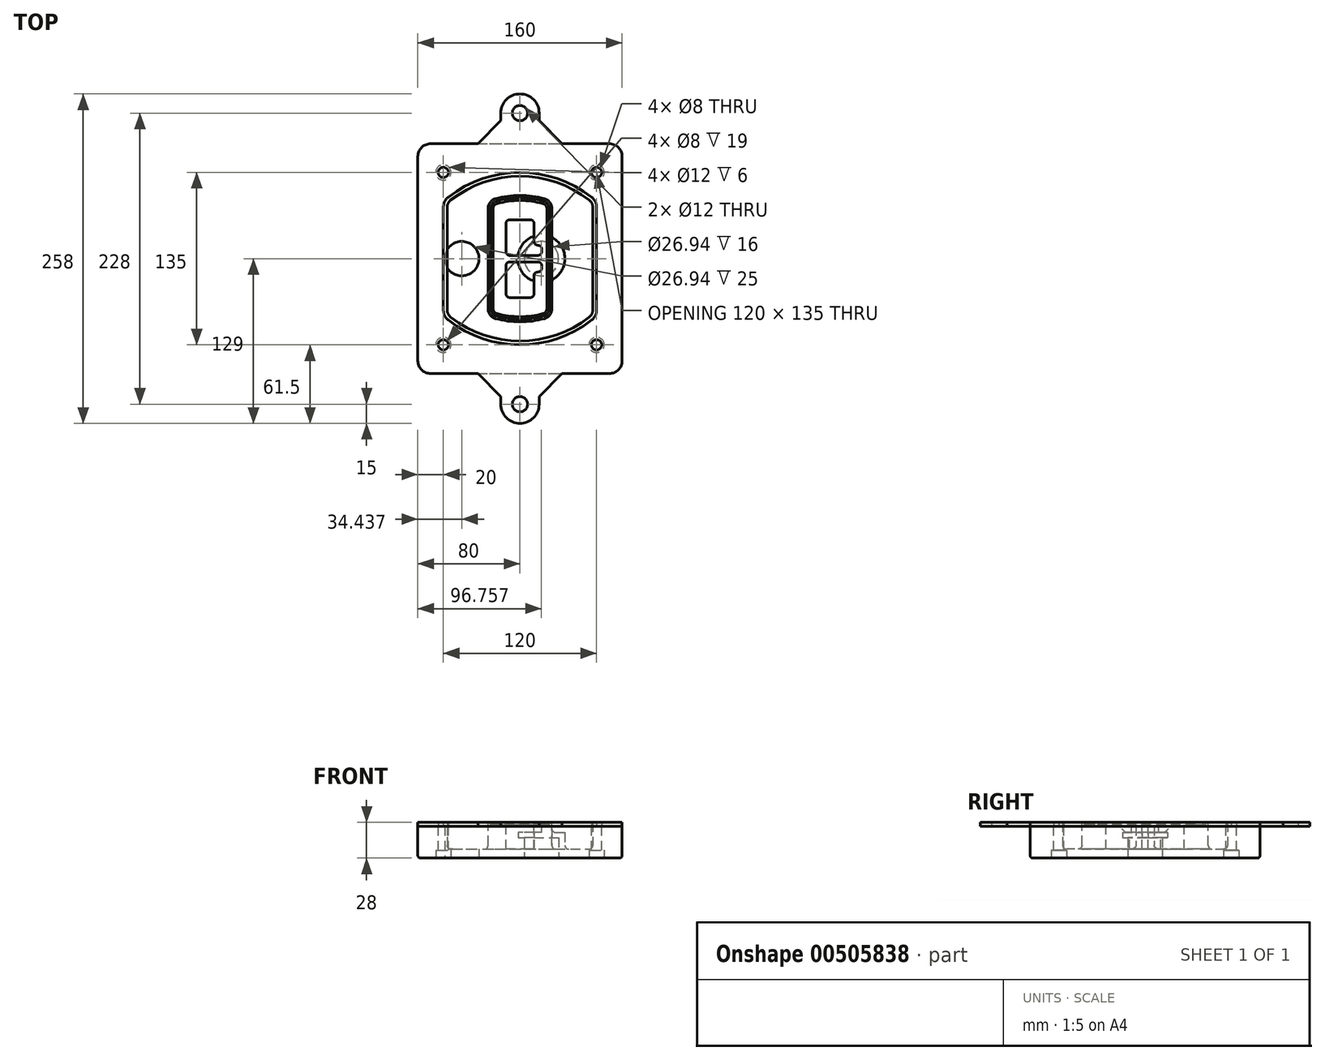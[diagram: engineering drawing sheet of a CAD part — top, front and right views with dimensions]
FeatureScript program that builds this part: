
annotation { "Feature Type Name" : "Feature", "Feature Type Description" : "" }
export const myFeature = defineFeature(function(context is Context, id is Id, definition is map)
    precondition{}
    {
        {
            var Q0;
            Q0=qCreatedBy(makeId("Top.planeOp"),FACE);
            var sketch = newSketch(context, id + "F0", { "sketchPlane" : qUnion([Q0])});
            skPoint(sketch, "E0.rect.middle", {"position": v(0, 0) * mm});
            skLineSegment(sketch, "E1.bottom", {"start": v(-70, -90) * mm, "end": v(70, -90) * mm});
            skLineSegment(sketch, "E1.top", {"start": v(-70, 90) * mm, "end": v(70, 90) * mm});
            skLineSegment(sketch, "E1.left", {"start": v(-80, -80) * mm, "end": v(-80, 80) * mm});
            skLineSegment(sketch, "E1.right", {"start": v(80, -80) * mm, "end": v(80, 80) * mm});
            skLineSegment(sketch, "E2", {"start": v(-80, 90) * mm, "end": v(80, -90) * mm, "construction": true});
            skLineSegment(sketch, "E3", {"start": v(80, 90) * mm, "end": v(-80, -90) * mm, "construction": true});
            skCircle(sketch, "E4", {"center": v(-60, 67.5) * mm, "radius": 4 * mm});
            skCircle(sketch, "E5", {"center": v(60, 67.5) * mm, "radius": 4 * mm});
            skCircle(sketch, "E6", {"center": v(60, -67.5) * mm, "radius": 4 * mm});
            skCircle(sketch, "E7", {"center": v(-60, -67.5) * mm, "radius": 4 * mm});
            skLineSegment(sketch, "E8", {"start": v(-60, 67.5) * mm, "end": v(60, 67.5) * mm, "construction": true});
            skLineSegment(sketch, "E9", {"start": v(60, 67.5) * mm, "end": v(60, -67.5) * mm, "construction": true});
            skLineSegment(sketch, "E10", {"start": v(60, -67.5) * mm, "end": v(-60, -67.5) * mm, "construction": true});
            skLineSegment(sketch, "E11", {"start": v(-60, -67.5) * mm, "end": v(-60, 67.5) * mm, "construction": true});
            skLineSegment(sketch, "E12", {"start": v(-60, 40.3) * mm, "end": v(-60, -40.3) * mm});
            skLineSegment(sketch, "E13", {"start": v(60, 40.3) * mm, "end": v(60, -40.3) * mm});
            skArc(sketch, "E14", {"start": v(56.15, 48.18) * mm, "mid": v(0, 67.5) * mm, "end": v(-56.15, 48.18) * mm});
            skArc(sketch, "E15", {"start": v(-56.15, -48.18) * mm, "mid": v(0, -67.5) * mm, "end": v(56.15, -48.18) * mm});
            skLineSegment(sketch, "E16", {"start": v(-60, 0) * mm, "end": v(60, 0) * mm, "construction": true});
            skPoint(sketch, "E17.visualSharp", {"position": v(-60, -45) * mm});
            skArc(sketch, "E17.filletArc", {"start": v(-60, -40.3) * mm, "mid": v(-58.99, -44.68) * mm, "end": v(-56.15, -48.18) * mm});
            skPoint(sketch, "E18.visualSharp", {"position": v(-60, 45) * mm});
            skArc(sketch, "E18.filletArc", {"start": v(-56.15, 48.18) * mm, "mid": v(-58.99, 44.68) * mm, "end": v(-60, 40.3) * mm});
            skPoint(sketch, "E19.visualSharp", {"position": v(60, 45) * mm});
            skArc(sketch, "E19.filletArc", {"start": v(60, 40.3) * mm, "mid": v(58.99, 44.68) * mm, "end": v(56.15, 48.18) * mm});
            skPoint(sketch, "E20.visualSharp", {"position": v(60, -45) * mm});
            skArc(sketch, "E20.filletArc", {"start": v(56.15, -48.18) * mm, "mid": v(58.99, -44.68) * mm, "end": v(60, -40.3) * mm});
            skPoint(sketch, "E21.visualSharp", {"position": v(-80, 90) * mm});
            skArc(sketch, "E21.filletArc", {"start": v(-70, 90) * mm, "mid": v(-77.07, 87.07) * mm, "end": v(-80, 80) * mm});
            skPoint(sketch, "E22.visualSharp", {"position": v(80, 90) * mm});
            skArc(sketch, "E22.filletArc", {"start": v(80, 80) * mm, "mid": v(77.07, 87.07) * mm, "end": v(70, 90) * mm});
            skPoint(sketch, "E23.visualSharp", {"position": v(80, -90) * mm});
            skArc(sketch, "E23.filletArc", {"start": v(70, -90) * mm, "mid": v(77.07, -87.07) * mm, "end": v(80, -80) * mm});
            skPoint(sketch, "E24.visualSharp", {"position": v(-80, -90) * mm});
            skArc(sketch, "E24.filletArc", {"start": v(-80, -80) * mm, "mid": v(-77.07, -87.07) * mm, "end": v(-70, -90) * mm});
            skArc(sketch, "E25.0", {"start": v(57, 40.3) * mm, "mid": v(56.3, 43.36) * mm, "end": v(54.3, 45.81) * mm});
            skLineSegment(sketch, "E25.1", {"start": v(57, 40.3) * mm, "end": v(57, -40.3) * mm});
            skArc(sketch, "E25.2", {"start": v(54.3, -45.81) * mm, "mid": v(56.3, -43.36) * mm, "end": v(57, -40.3) * mm});
            skArc(sketch, "E25.3", {"start": v(-54.3, -45.81) * mm, "mid": v(0, -64.5) * mm, "end": v(54.3, -45.81) * mm});
            skArc(sketch, "E25.4", {"start": v(-57, -40.3) * mm, "mid": v(-56.3, -43.36) * mm, "end": v(-54.3, -45.81) * mm});
            skArc(sketch, "E25.5", {"start": v(54.3, 45.81) * mm, "mid": v(0, 64.5) * mm, "end": v(-54.3, 45.81) * mm});
            skLineSegment(sketch, "E25.6", {"start": v(-57, 40.3) * mm, "end": v(-57, -40.3) * mm});
            skArc(sketch, "E25.7", {"start": v(-54.3, 45.81) * mm, "mid": v(-56.3, 43.36) * mm, "end": v(-57, 40.3) * mm});
            skArc(sketch, "E26.0", {"start": v(-58.62, 51.33) * mm, "mid": v(-62.58, 46.43) * mm, "end": v(-64, 40.3) * mm});
            skArc(sketch, "E26.1", {"start": v(58.62, 51.33) * mm, "mid": v(0, 71.5) * mm, "end": v(-58.62, 51.33) * mm});
            skArc(sketch, "E26.2", {"start": v(64, 40.3) * mm, "mid": v(62.58, 46.43) * mm, "end": v(58.62, 51.33) * mm});
            skLineSegment(sketch, "E26.3", {"start": v(64, 40.3) * mm, "end": v(64, -40.3) * mm});
            skArc(sketch, "E26.4", {"start": v(58.62, -51.33) * mm, "mid": v(62.58, -46.43) * mm, "end": v(64, -40.3) * mm});
            skLineSegment(sketch, "E26.5", {"start": v(-64, 40.3) * mm, "end": v(-64, -40.3) * mm});
            skArc(sketch, "E26.6", {"start": v(-58.62, -51.33) * mm, "mid": v(0, -71.5) * mm, "end": v(58.62, -51.33) * mm});
            skArc(sketch, "E26.7", {"start": v(-64, -40.3) * mm, "mid": v(-62.58, -46.43) * mm, "end": v(-58.62, -51.33) * mm});
            skSolve(sketch);
        }
        {
            var Q0;
            Q0=makeQuery(id+"F0.imprint","IMPRINT",FACE,{"disambiguationData":[TD([[makeQuery(id+"F0.imprint","IMPRINT",EDGE,{"derivedFrom":sQuery(id+"F0.wireOp",EDGE,"E1.bottom")}),1.0]])]});
            var Q1;
            Q1=makeQuery(id+"F0.imprint","IMPRINT",FACE,{"disambiguationData":[TD([[makeQuery(id+"F0.imprint","IMPRINT",EDGE,{"derivedFrom":sQuery(id+"F0.wireOp",EDGE,"E12")}),1.0]])]});
            var Q2;
            Q2=makeQuery(id+"F0.imprint","IMPRINT",FACE,{"disambiguationData":[TD([[makeQuery(id+"F0.imprint","IMPRINT",EDGE,{"derivedFrom":sQuery(id+"F0.wireOp",EDGE,"E25.0")}),1.0]])]});
            var Q3;
            Q3=makeQuery(id+"F0.imprint","IMPRINT",FACE,{"disambiguationData":[TD([[makeQuery(id+"F0.imprint","IMPRINT",EDGE,{"derivedFrom":sQuery(id+"F0.wireOp",EDGE,"E12")}),-1.0]])]});
            extrude(context, id + "F1", {"entities" : qUnion([Q0, Q1, Q2, Q3]), "oppositeDirection" : true, "depth" : 25 * mm});
        }
        {
            var Q0;
            Q0=makeQuery(id+"F0.imprint","IMPRINT",FACE,{"disambiguationData":[TD([[makeQuery(id+"F0.imprint","IMPRINT",EDGE,{"derivedFrom":sQuery(id+"F0.wireOp",EDGE,"E12")}),1.0]])]});
            extrude(context, id + "F2", {"entities" : qUnion([Q0]), "operationType" : NewBodyOperationType.ADD, "depth" : 3 * mm});
        }
        {
            var Q0;
            Q0=makeQuery(id+"F0.imprint","IMPRINT",FACE,{"disambiguationData":[TD([[makeQuery(id+"F0.imprint","IMPRINT",EDGE,{"derivedFrom":sQuery(id+"F0.wireOp",EDGE,"E25.0")}),1.0]])]});
            extrude(context, id + "F3", {"entities" : qUnion([Q0]), "operationType" : NewBodyOperationType.REMOVE, "oppositeDirection" : true, "depth" : 18 * mm});
        }
        {
            var Q0;
            Q0=makeQuery(id+"F2.opExtrude","CAP_FACE",FACE,{"disambiguationData":[OSD([sQuery(id+"F0.wireOp",EDGE,"E12"),sQuery(id+"F0.wireOp",EDGE,"E13"),sQuery(id+"F0.wireOp",EDGE,"E14"),sQuery(id+"F0.wireOp",EDGE,"E15"),sQuery(id+"F0.wireOp",EDGE,"E17.filletArc"),sQuery(id+"F0.wireOp",EDGE,"E18.filletArc"),sQuery(id+"F0.wireOp",EDGE,"E19.filletArc"),sQuery(id+"F0.wireOp",EDGE,"E20.filletArc"),sQuery(id+"F0.wireOp",EDGE,"E25.0"),sQuery(id+"F0.wireOp",EDGE,"E25.1"),sQuery(id+"F0.wireOp",EDGE,"E25.2"),sQuery(id+"F0.wireOp",EDGE,"E25.3"),sQuery(id+"F0.wireOp",EDGE,"E25.4"),sQuery(id+"F0.wireOp",EDGE,"E25.5"),sQuery(id+"F0.wireOp",EDGE,"E25.6"),sQuery(id+"F0.wireOp",EDGE,"E25.7")])],"isStart":false});
            var sketch = newSketch(context, id + "F4", { "sketchPlane" : qUnion([Q0])});
            skArc(sketch, "E27.0", {"start": v(-19.08, -46.97) * mm, "mid": v(0, -49.5) * mm, "end": v(19.08, -46.97) * mm});
            skArc(sketch, "E28.0", {"start": v(19.08, 46.97) * mm, "mid": v(0, 49.5) * mm, "end": v(-19.08, 46.97) * mm});
            skLineSegment(sketch, "E29", {"start": v(-25, 39.25) * mm, "end": v(-25, -39.25) * mm});
            skLineSegment(sketch, "E30", {"start": v(25, 39.25) * mm, "end": v(25, -39.25) * mm});
            skLineSegment(sketch, "E31", {"start": v(-25, 45.1) * mm, "end": v(25, 45.1) * mm, "construction": true});
            skLineSegment(sketch, "E32", {"start": v(-25, -45.1) * mm, "end": v(25, -45.1) * mm, "construction": true});
            skPoint(sketch, "E33.visualSharp", {"position": v(-25, 45.1) * mm});
            skArc(sketch, "E33.filletArc", {"start": v(-19.08, 46.97) * mm, "mid": v(-23.35, 44.11) * mm, "end": v(-25, 39.25) * mm});
            skPoint(sketch, "E34.visualSharp", {"position": v(25, 45.1) * mm});
            skArc(sketch, "E34.filletArc", {"start": v(25, 39.25) * mm, "mid": v(23.35, 44.11) * mm, "end": v(19.08, 46.97) * mm});
            skPoint(sketch, "E35.visualSharp", {"position": v(25, -45.1) * mm});
            skArc(sketch, "E35.filletArc", {"start": v(19.08, -46.97) * mm, "mid": v(23.35, -44.11) * mm, "end": v(25, -39.25) * mm});
            skPoint(sketch, "E36.visualSharp", {"position": v(-25, -45.1) * mm});
            skArc(sketch, "E36.filletArc", {"start": v(-25, -39.25) * mm, "mid": v(-23.35, -44.11) * mm, "end": v(-19.08, -46.97) * mm});
            skArc(sketch, "E37.0", {"start": v(54.3, 45.81) * mm, "mid": v(0, 64.5) * mm, "end": v(-54.3, 45.81) * mm});
            skArc(sketch, "E37.1", {"start": v(-54.3, 45.81) * mm, "mid": v(-56.3, 43.36) * mm, "end": v(-57, 40.3) * mm});
            skLineSegment(sketch, "E37.2", {"start": v(-57, 40.3) * mm, "end": v(-57, -40.3) * mm});
            skArc(sketch, "E37.3", {"start": v(-57, -40.3) * mm, "mid": v(-56.3, -43.36) * mm, "end": v(-54.3, -45.81) * mm});
            skArc(sketch, "E37.4", {"start": v(-54.3, -45.81) * mm, "mid": v(0, -64.5) * mm, "end": v(54.3, -45.81) * mm});
            skArc(sketch, "E37.5", {"start": v(54.3, -45.81) * mm, "mid": v(56.3, -43.36) * mm, "end": v(57, -40.3) * mm});
            skLineSegment(sketch, "E37.6", {"start": v(57, 40.3) * mm, "end": v(57, -40.3) * mm});
            skArc(sketch, "E37.7", {"start": v(57, 40.3) * mm, "mid": v(56.3, 43.36) * mm, "end": v(54.3, 45.81) * mm});
            skLineSegment(sketch, "E38.0", {"start": v(23, 39.25) * mm, "end": v(23, -39.25) * mm});
            skArc(sketch, "E38.1", {"start": v(18.56, -45.04) * mm, "mid": v(21.76, -42.9) * mm, "end": v(23, -39.25) * mm});
            skArc(sketch, "E38.2", {"start": v(-18.56, -45.04) * mm, "mid": v(0, -47.5) * mm, "end": v(18.56, -45.04) * mm});
            skArc(sketch, "E38.3", {"start": v(-23, -39.25) * mm, "mid": v(-21.76, -42.9) * mm, "end": v(-18.56, -45.04) * mm});
            skLineSegment(sketch, "E38.4", {"start": v(-23, 39.25) * mm, "end": v(-23, -39.25) * mm});
            skArc(sketch, "E38.5", {"start": v(23, 39.25) * mm, "mid": v(21.76, 42.9) * mm, "end": v(18.56, 45.04) * mm});
            skArc(sketch, "E38.6", {"start": v(-18.56, 45.04) * mm, "mid": v(-21.76, 42.9) * mm, "end": v(-23, 39.25) * mm});
            skArc(sketch, "E38.7", {"start": v(18.56, 45.04) * mm, "mid": v(0, 47.5) * mm, "end": v(-18.56, 45.04) * mm});
            skArc(sketch, "E39.0", {"start": v(21, 39.25) * mm, "mid": v(20.18, 41.68) * mm, "end": v(18.04, 43.1) * mm});
            skLineSegment(sketch, "E39.1", {"start": v(21, 39.25) * mm, "end": v(21, -39.25) * mm});
            skArc(sketch, "E39.2", {"start": v(18.04, -43.1) * mm, "mid": v(20.18, -41.68) * mm, "end": v(21, -39.25) * mm});
            skArc(sketch, "E39.3", {"start": v(-18.04, -43.1) * mm, "mid": v(0, -45.5) * mm, "end": v(18.04, -43.1) * mm});
            skArc(sketch, "E39.4", {"start": v(-21, -39.25) * mm, "mid": v(-20.18, -41.68) * mm, "end": v(-18.04, -43.1) * mm});
            skArc(sketch, "E39.5", {"start": v(18.04, 43.1) * mm, "mid": v(0, 45.5) * mm, "end": v(-18.04, 43.1) * mm});
            skLineSegment(sketch, "E39.6", {"start": v(-21, 39.25) * mm, "end": v(-21, -39.25) * mm});
            skArc(sketch, "E39.7", {"start": v(-18.04, 43.1) * mm, "mid": v(-20.18, 41.68) * mm, "end": v(-21, 39.25) * mm});
            skLineSegment(sketch, "E40", {"start": v(-25, 0) * mm, "end": v(25, 0) * mm, "construction": true});
            skLineSegment(sketch, "E41", {"start": v(-11, 5.5) * mm, "end": v(-11, 27.5) * mm});
            skLineSegment(sketch, "E42", {"start": v(-8, 30.5) * mm, "end": v(8, 30.5) * mm});
            skLineSegment(sketch, "E43", {"start": v(11, 27.5) * mm, "end": v(11, 13.5) * mm});
            skLineSegment(sketch, "E44", {"start": v(14, 10.5) * mm, "end": v(14, 10.5) * mm});
            skLineSegment(sketch, "E45", {"start": v(17, 7.5) * mm, "end": v(17, 5.5) * mm});
            skLineSegment(sketch, "E46", {"start": v(14, 2.5) * mm, "end": v(-8, 2.5) * mm});
            skPoint(sketch, "E47.visualSharp", {"position": v(-11, 30.5) * mm});
            skArc(sketch, "E47.filletArc", {"start": v(-8, 30.5) * mm, "mid": v(-10.12, 29.62) * mm, "end": v(-11, 27.5) * mm});
            skPoint(sketch, "E48.visualSharp", {"position": v(11, 30.5) * mm});
            skArc(sketch, "E48.filletArc", {"start": v(11, 27.5) * mm, "mid": v(10.12, 29.62) * mm, "end": v(8, 30.5) * mm});
            skPoint(sketch, "E49.visualSharp", {"position": v(11, 10.5) * mm});
            skArc(sketch, "E49.filletArc", {"start": v(11, 13.5) * mm, "mid": v(11.88, 11.38) * mm, "end": v(14, 10.5) * mm});
            skPoint(sketch, "E50.visualSharp", {"position": v(17, 10.5) * mm});
            skArc(sketch, "E50.filletArc", {"start": v(17, 7.5) * mm, "mid": v(16.12, 9.62) * mm, "end": v(14, 10.5) * mm});
            skPoint(sketch, "E51.visualSharp", {"position": v(17, 2.5) * mm});
            skArc(sketch, "E51.filletArc", {"start": v(14, 2.5) * mm, "mid": v(16.12, 3.38) * mm, "end": v(17, 5.5) * mm});
            skPoint(sketch, "E52.visualSharp", {"position": v(-11, 2.5) * mm});
            skArc(sketch, "E52.filletArc", {"start": v(-11, 5.5) * mm, "mid": v(-10.12, 3.38) * mm, "end": v(-8, 2.5) * mm});
            skLineSegment(sketch, "E53.0.MirrorCS", {"start": v(14, -2.5) * mm, "end": v(-8, -2.5) * mm});
            skArc(sketch, "E54.0.MirrorCS", {"start": v(-11, -5.5) * mm, "mid": v(-10.12, -3.38) * mm, "end": v(-8, -2.5) * mm});
            skLineSegment(sketch, "E55.0.MirrorCS", {"start": v(-11, -5.5) * mm, "end": v(-11, -27.5) * mm});
            skArc(sketch, "E56.0.MirrorCS", {"start": v(-8, -30.5) * mm, "mid": v(-10.12, -29.62) * mm, "end": v(-11, -27.5) * mm});
            skLineSegment(sketch, "E57.0.MirrorCS", {"start": v(-8, -30.5) * mm, "end": v(8, -30.5) * mm});
            skArc(sketch, "E58.0.MirrorCS", {"start": v(11, -27.5) * mm, "mid": v(10.12, -29.62) * mm, "end": v(8, -30.5) * mm});
            skLineSegment(sketch, "E59.0.MirrorCS", {"start": v(11, -27.5) * mm, "end": v(11, -13.5) * mm});
            skArc(sketch, "E60.0.MirrorCS", {"start": v(11, -13.5) * mm, "mid": v(11.88, -11.38) * mm, "end": v(14, -10.5) * mm});
            skArc(sketch, "E61.0.MirrorCS", {"start": v(17, -7.5) * mm, "mid": v(16.12, -9.62) * mm, "end": v(14, -10.5) * mm});
            skLineSegment(sketch, "E62.0.MirrorCS", {"start": v(17, -7.5) * mm, "end": v(17, -5.5) * mm});
            skArc(sketch, "E63.0.MirrorCS", {"start": v(14, -2.5) * mm, "mid": v(16.12, -3.38) * mm, "end": v(17, -5.5) * mm});
            skSolve(sketch);
        }
        {
            var Q0;
            Q0=makeQuery(id+"F4.imprint","IMPRINT",FACE,{"disambiguationData":[TD([[makeQuery(id+"F4.imprint","IMPRINT",EDGE,{"derivedFrom":sQuery(id+"F4.wireOp",EDGE,"E27.0")}),1.0]])]});
            var Q1;
            Q1=makeQuery(id+"F4.imprint","IMPRINT",FACE,{"disambiguationData":[TD([[makeQuery(id+"F4.imprint","IMPRINT",EDGE,{"derivedFrom":sQuery(id+"F4.wireOp",EDGE,"E38.0")}),-1.0]])]});
            var Q2;
            Q2=makeQuery(id+"F4.imprint","IMPRINT",FACE,{"disambiguationData":[TD([[makeQuery(id+"F4.imprint","IMPRINT",EDGE,{"derivedFrom":sQuery(id+"F4.wireOp",EDGE,"E39.0")}),1.0]])]});
            extrude(context, id + "F5", {"entities" : qUnion([Q0, Q1, Q2]), "operationType" : NewBodyOperationType.ADD, "endBound" : BoundingType.UP_TO_NEXT, "oppositeDirection" : true, "depth" : 25 * mm});
        }
        {
            var Q0;
            Q0=makeQuery(id+"F4.imprint","IMPRINT",FACE,{"disambiguationData":[TD([[makeQuery(id+"F4.imprint","IMPRINT",EDGE,{"derivedFrom":sQuery(id+"F4.wireOp",EDGE,"E38.0")}),-1.0]])]});
            extrude(context, id + "F6", {"entities" : qUnion([Q0]), "operationType" : NewBodyOperationType.REMOVE, "oppositeDirection" : true, "depth" : 2 * mm});
        }
        {
            var Q0;
            Q0=makeQuery(id+"F1.opExtrude","CAP_FACE",FACE,{"disambiguationData":[OSD([sQuery(id+"F0.wireOp",EDGE,"E1.bottom"),sQuery(id+"F0.wireOp",EDGE,"E1.top"),sQuery(id+"F0.wireOp",EDGE,"E1.left"),sQuery(id+"F0.wireOp",EDGE,"E1.right"),sQuery(id+"F0.wireOp",EDGE,"E4"),sQuery(id+"F0.wireOp",EDGE,"E5"),sQuery(id+"F0.wireOp",EDGE,"E6"),sQuery(id+"F0.wireOp",EDGE,"E7"),sQuery(id+"F0.wireOp",EDGE,"E21.filletArc"),sQuery(id+"F0.wireOp",EDGE,"E22.filletArc"),sQuery(id+"F0.wireOp",EDGE,"E23.filletArc"),sQuery(id+"F0.wireOp",EDGE,"E24.filletArc")])],"isStart":false});
            var sketch = newSketch(context, id + "F7", { "sketchPlane" : qUnion([Q0])});
            skCircle(sketch, "E64", {"center": v(16.76, 0) * mm, "radius": 13.47 * mm});
            skCircle(sketch, "E65", {"center": v(-45.56, 0) * mm, "radius": 13.47 * mm});
            skLineSegment(sketch, "E66", {"start": v(80, 0) * mm, "end": v(-80, 0) * mm});
            skCircle(sketch, "E67", {"center": v(16.76, 0) * mm, "radius": 18.47 * mm});
            skCircle(sketch, "E68", {"center": v(60, -67.5) * mm, "radius": 6 * mm});
            skCircle(sketch, "E69", {"center": v(-60, -67.5) * mm, "radius": 6 * mm});
            skCircle(sketch, "E70", {"center": v(-60, 67.5) * mm, "radius": 6 * mm});
            skCircle(sketch, "E71", {"center": v(60, 67.5) * mm, "radius": 6 * mm});
            skSolve(sketch);
        }
        {
            var Q0;
            {var subQ1=sQuery(id+"F7.wireOp",EDGE,"E66");var subQ4=sQuery(id+"F7.wireOp",EDGE,"E64");var subQ6=makeQuery(id+"F7.imprint","INTERSECT",VERTEX,{"disambiguationData":[OD(0.0)],"derivedFrom":[subQ4,subQ1]});Q0=makeQuery(id+"F7.imprint","IMPRINT",FACE,{"disambiguationData":[TD([[makeQuery(id+"F7.imprint","IMPRINT",EDGE,{"disambiguationData":[TD([[subQ6,-1.0]])],"derivedFrom":subQ4}),-1.0]])]});}
            var Q1;
            {var subQ0=sQuery(id+"F7.wireOp",EDGE,"E66");var subQ1=sQuery(id+"F7.wireOp",EDGE,"E64");var subQ3=makeQuery(id+"F7.imprint","INTERSECT",VERTEX,{"disambiguationData":[OD(0.0)],"derivedFrom":[subQ1,subQ0]});Q1=makeQuery(id+"F7.imprint","IMPRINT",FACE,{"disambiguationData":[TD([[makeQuery(id+"F7.imprint","IMPRINT",EDGE,{"disambiguationData":[TD([[subQ3,-1.0]])],"derivedFrom":subQ1}),1.0]])]});}
            var Q2;
            {var subQ0=sQuery(id+"F7.wireOp",EDGE,"E66");var subQ1=sQuery(id+"F7.wireOp",EDGE,"E64");var subQ3=makeQuery(id+"F7.imprint","INTERSECT",VERTEX,{"disambiguationData":[OD(0.0)],"derivedFrom":[subQ1,subQ0]});Q2=makeQuery(id+"F7.imprint","IMPRINT",FACE,{"disambiguationData":[TD([[makeQuery(id+"F7.imprint","IMPRINT",EDGE,{"disambiguationData":[TD([[subQ3,1.0]])],"derivedFrom":subQ1}),1.0]])]});}
            var Q3;
            {var subQ1=sQuery(id+"F7.wireOp",EDGE,"E66");var subQ4=sQuery(id+"F7.wireOp",EDGE,"E64");var subQ6=makeQuery(id+"F7.imprint","INTERSECT",VERTEX,{"disambiguationData":[OD(0.0)],"derivedFrom":[subQ4,subQ1]});Q3=makeQuery(id+"F7.imprint","IMPRINT",FACE,{"disambiguationData":[TD([[makeQuery(id+"F7.imprint","IMPRINT",EDGE,{"disambiguationData":[TD([[subQ6,1.0]])],"derivedFrom":subQ4}),-1.0]])]});}
            extrude(context, id + "F8", {"entities" : qUnion([Q0, Q1, Q2, Q3]), "operationType" : NewBodyOperationType.ADD, "oppositeDirection" : true, "depth" : 20 * mm});
        }
        {
            var Q0;
            {var subQ0=sQuery(id+"F7.wireOp",EDGE,"E66");var subQ1=sQuery(id+"F7.wireOp",EDGE,"E64");var subQ3=makeQuery(id+"F7.imprint","INTERSECT",VERTEX,{"disambiguationData":[OD(0.0)],"derivedFrom":[subQ1,subQ0]});Q0=makeQuery(id+"F7.imprint","IMPRINT",FACE,{"disambiguationData":[TD([[makeQuery(id+"F7.imprint","IMPRINT",EDGE,{"disambiguationData":[TD([[subQ3,-1.0]])],"derivedFrom":subQ1}),1.0]])]});}
            var Q1;
            {var subQ0=sQuery(id+"F7.wireOp",EDGE,"E66");var subQ1=sQuery(id+"F7.wireOp",EDGE,"E64");var subQ3=makeQuery(id+"F7.imprint","INTERSECT",VERTEX,{"disambiguationData":[OD(0.0)],"derivedFrom":[subQ1,subQ0]});Q1=makeQuery(id+"F7.imprint","IMPRINT",FACE,{"disambiguationData":[TD([[makeQuery(id+"F7.imprint","IMPRINT",EDGE,{"disambiguationData":[TD([[subQ3,1.0]])],"derivedFrom":subQ1}),1.0]])]});}
            extrude(context, id + "F9", {"entities" : qUnion([Q0, Q1]), "operationType" : NewBodyOperationType.REMOVE, "oppositeDirection" : true, "depth" : 16 * mm});
        }
        {
            var Q0;
            {var subQ0=sQuery(id+"F7.wireOp",EDGE,"E66");var subQ1=sQuery(id+"F7.wireOp",EDGE,"E65");var subQ3=makeQuery(id+"F7.imprint","INTERSECT",VERTEX,{"disambiguationData":[OD(0.0)],"derivedFrom":[subQ1,subQ0]});Q0=makeQuery(id+"F7.imprint","IMPRINT",FACE,{"disambiguationData":[TD([[makeQuery(id+"F7.imprint","IMPRINT",EDGE,{"disambiguationData":[TD([[subQ3,-1.0]])],"derivedFrom":subQ1}),1.0]])]});}
            var Q1;
            {var subQ0=sQuery(id+"F7.wireOp",EDGE,"E66");var subQ1=sQuery(id+"F7.wireOp",EDGE,"E65");var subQ3=makeQuery(id+"F7.imprint","INTERSECT",VERTEX,{"disambiguationData":[OD(0.0)],"derivedFrom":[subQ1,subQ0]});Q1=makeQuery(id+"F7.imprint","IMPRINT",FACE,{"disambiguationData":[TD([[makeQuery(id+"F7.imprint","IMPRINT",EDGE,{"disambiguationData":[TD([[subQ3,1.0]])],"derivedFrom":subQ1}),1.0]])]});}
            extrude(context, id + "F10", {"entities" : qUnion([Q0, Q1]), "operationType" : NewBodyOperationType.REMOVE, "oppositeDirection" : true, "depth" : 25 * mm});
        }
        {
            var Q0;
            Q0=makeQuery(id+"F7.imprint","IMPRINT",FACE,{"disambiguationData":[TD([[makeQuery(id+"F7.imprint","IMPRINT",EDGE,{"derivedFrom":sQuery(id+"F7.wireOp",EDGE,"E68")}),1.0]])]});
            var Q1;
            Q1=makeQuery(id+"F7.imprint","IMPRINT",FACE,{"disambiguationData":[TD([[makeQuery(id+"F7.imprint","IMPRINT",EDGE,{"derivedFrom":makeQuery(id+"F1.opExtrude","CAP_EDGE",EDGE,{"disambiguationData":[OSD([sQuery(id+"F0.wireOp",EDGE,"E5")])],"isStart":false})}),-1.0]])]});
            var Q2;
            Q2=makeQuery(id+"F7.imprint","IMPRINT",FACE,{"disambiguationData":[TD([[makeQuery(id+"F7.imprint","IMPRINT",EDGE,{"derivedFrom":sQuery(id+"F7.wireOp",EDGE,"E69")}),1.0]])]});
            var Q3;
            Q3=makeQuery(id+"F7.imprint","IMPRINT",FACE,{"disambiguationData":[TD([[makeQuery(id+"F7.imprint","IMPRINT",EDGE,{"derivedFrom":makeQuery(id+"F1.opExtrude","CAP_EDGE",EDGE,{"disambiguationData":[OSD([sQuery(id+"F0.wireOp",EDGE,"E4")])],"isStart":false})}),-1.0]])]});
            var Q4;
            Q4=makeQuery(id+"F7.imprint","IMPRINT",FACE,{"disambiguationData":[TD([[makeQuery(id+"F7.imprint","IMPRINT",EDGE,{"derivedFrom":sQuery(id+"F7.wireOp",EDGE,"E70")}),1.0]])]});
            var Q5;
            Q5=makeQuery(id+"F7.imprint","IMPRINT",FACE,{"disambiguationData":[TD([[makeQuery(id+"F7.imprint","IMPRINT",EDGE,{"derivedFrom":makeQuery(id+"F1.opExtrude","CAP_EDGE",EDGE,{"disambiguationData":[OSD([sQuery(id+"F0.wireOp",EDGE,"E7")])],"isStart":false})}),-1.0]])]});
            var Q6;
            Q6=makeQuery(id+"F7.imprint","IMPRINT",FACE,{"disambiguationData":[TD([[makeQuery(id+"F7.imprint","IMPRINT",EDGE,{"derivedFrom":sQuery(id+"F7.wireOp",EDGE,"E71")}),1.0]])]});
            var Q7;
            Q7=makeQuery(id+"F7.imprint","IMPRINT",FACE,{"disambiguationData":[TD([[makeQuery(id+"F7.imprint","IMPRINT",EDGE,{"derivedFrom":makeQuery(id+"F1.opExtrude","CAP_EDGE",EDGE,{"disambiguationData":[OSD([sQuery(id+"F0.wireOp",EDGE,"E6")])],"isStart":false})}),-1.0]])]});
            extrude(context, id + "F11", {"entities" : qUnion([Q0, Q1, Q2, Q3, Q4, Q5, Q6, Q7]), "operationType" : NewBodyOperationType.REMOVE, "oppositeDirection" : true, "depth" : 6 * mm});
        }
        {
            var Q0;
            Q0=makeQuery(id+"F9.boolean.opBoolean","COPY",FACE,{"derivedFrom":makeQuery(id+"F9.opExtrude","CAP_FACE",FACE,{"disambiguationData":[OSD([sQuery(id+"F7.wireOp",EDGE,"E64")])],"isStart":false})});
            var sketch = newSketch(context, id + "F12", { "sketchPlane" : qUnion([Q0])});
            skArc(sketch, "E72.0", {"start": v(11, 17.55) * mm, "mid": v(2.57, 11.82) * mm, "end": v(-1.54, 2.5) * mm});
            skArc(sketch, "E72.1", {"start": v(-1.54, -2.5) * mm, "mid": v(2.57, -11.82) * mm, "end": v(11, -17.55) * mm});
            skLineSegment(sketch, "E73", {"start": v(-1.54, -2.5) * mm, "end": v(14, -2.5) * mm});
            skLineSegment(sketch, "E74.0", {"start": v(14, 2.5) * mm, "end": v(-1.54, 2.5) * mm});
            skArc(sketch, "E74.1", {"start": v(14, 2.5) * mm, "mid": v(16.12, 3.38) * mm, "end": v(17, 5.5) * mm});
            skLineSegment(sketch, "E74.2", {"start": v(17, 7.5) * mm, "end": v(17, 5.5) * mm});
            skArc(sketch, "E74.3", {"start": v(17, 7.5) * mm, "mid": v(16.12, 9.62) * mm, "end": v(14, 10.5) * mm});
            skArc(sketch, "E74.4", {"start": v(11, 13.5) * mm, "mid": v(11.88, 11.38) * mm, "end": v(14, 10.5) * mm});
            skLineSegment(sketch, "E74.5", {"start": v(11, 17.55) * mm, "end": v(11, 13.5) * mm});
            skLineSegment(sketch, "E74.7", {"start": v(14, -2.5) * mm, "end": v(-1.54, -2.5) * mm});
            skArc(sketch, "E74.8", {"start": v(14, -2.5) * mm, "mid": v(16.12, -3.38) * mm, "end": v(17, -5.5) * mm});
            skLineSegment(sketch, "E74.9", {"start": v(17, -7.5) * mm, "end": v(17, -5.5) * mm});
            skArc(sketch, "E74.10", {"start": v(17, -7.5) * mm, "mid": v(16.12, -9.62) * mm, "end": v(14, -10.5) * mm});
            skArc(sketch, "E74.11", {"start": v(11, -13.5) * mm, "mid": v(11.88, -11.38) * mm, "end": v(14, -10.5) * mm});
            skLineSegment(sketch, "E74.12", {"start": v(11, -17.55) * mm, "end": v(11, -13.5) * mm});
            skPoint(sketch, "E75.orphan", {"position": v(11, -27.5) * mm});
            skPoint(sketch, "E76.orphan", {"position": v(-8, -2.5) * mm});
            skPoint(sketch, "E77.orphan", {"position": v(-8, 2.5) * mm});
            skPoint(sketch, "E78.orphan", {"position": v(11, 27.5) * mm});
            skSolve(sketch);
        }
        {
            var Q0;
            {var subQ7=sQuery(id+"F12.wireOp",EDGE,"E72.0");var subQ14=sQuery(id+"F12.wireOp",EDGE,"E72.1");var subQ16=sQuery(id+"F12.wireOp",EDGE,"E74.1");var subQ18=sQuery(id+"F12.wireOp",EDGE,"E74.8");Q0=qUnion([makeQuery(id+"F12.imprint","IMPRINT",FACE,{"disambiguationData":[TD([[makeQuery(id+"F12.imprint","IMPRINT",EDGE,{"derivedFrom":subQ7}),1.0]])]}),makeQuery(id+"F12.imprint","IMPRINT",FACE,{"disambiguationData":[TD([[makeQuery(id+"F12.imprint","IMPRINT",EDGE,{"derivedFrom":subQ14}),1.0]])]}),makeQuery(id+"F12.imprint","IMPRINT",FACE,{"disambiguationData":[TD([[makeQuery(id+"F12.imprint","IMPRINT",EDGE,{"derivedFrom":subQ16}),1.0]])]}),makeQuery(id+"F12.imprint","IMPRINT",FACE,{"disambiguationData":[TD([[makeQuery(id+"F12.imprint","IMPRINT",EDGE,{"derivedFrom":subQ18}),-1.0]])]})]);}
            var Q1;
            Q1=makeQuery(id+"F5.boolean.opBoolean","SPLIT",FACE,{"disambiguationData":[TD([makeQuery(id+"F5.opExtrude","SWEPT_FACE",FACE,{"disambiguationData":[OSD([sQuery(id+"F4.wireOp",EDGE,"E41")])]})])],"derivedFrom":makeQuery(id+"F3.boolean.opBoolean","COPY",FACE,{"derivedFrom":makeQuery(id+"F3.opExtrude","CAP_FACE",FACE,{"disambiguationData":[OSD([sQuery(id+"F0.wireOp",EDGE,"E25.0"),sQuery(id+"F0.wireOp",EDGE,"E25.1"),sQuery(id+"F0.wireOp",EDGE,"E25.2"),sQuery(id+"F0.wireOp",EDGE,"E25.3"),sQuery(id+"F0.wireOp",EDGE,"E25.4"),sQuery(id+"F0.wireOp",EDGE,"E25.5"),sQuery(id+"F0.wireOp",EDGE,"E25.6"),sQuery(id+"F0.wireOp",EDGE,"E25.7")])],"isStart":false})})});
            extrude(context, id + "F13", {"entities" : qUnion([Q0]), "operationType" : NewBodyOperationType.REMOVE, "endBound" : BoundingType.UP_TO_SURFACE, "endBoundEntityFace" : qUnion([Q1]), "depth" : 25 * mm});
        }
        {
            var Q0;
            Q0=makeQuery(id+"F3.boolean.opBoolean","COPY",EDGE,{"derivedFrom":makeQuery(id+"F3.opExtrude","CAP_EDGE",EDGE,{"disambiguationData":[OSD([sQuery(id+"F0.wireOp",EDGE,"E25.6")])],"isStart":false})});
            var Q1;
            Q1=makeQuery(id+"F8.boolean.opBoolean","INTERSECT",EDGE,{"derivedFrom":[makeQuery(id+"F5.opExtrude","SWEPT_FACE",FACE,{"disambiguationData":[OSD([sQuery(id+"F4.wireOp",EDGE,"E30")])]}),makeQuery(id+"F8.opExtrude","CAP_FACE",FACE,{"disambiguationData":[OSD([sQuery(id+"F7.wireOp",EDGE,"E67")])],"isStart":false})]});
            var Q2;
            Q2=makeQuery(id+"F8.boolean.opBoolean","INTERSECT",EDGE,{"disambiguationData":[OD(1.0)],"derivedFrom":[makeQuery(id+"F5.opExtrude","SWEPT_FACE",FACE,{"disambiguationData":[OSD([sQuery(id+"F4.wireOp",EDGE,"E30")])]}),makeQuery(id+"F8.opExtrude","SWEPT_FACE",FACE,{"disambiguationData":[OSD([sQuery(id+"F7.wireOp",EDGE,"E67")])]})]});
            var Q3;
            {var subQ0=sQuery(id+"F4.wireOp",EDGE,"E30");Q3=makeQuery(id+"F8.boolean.opBoolean","SPLIT",EDGE,{"disambiguationData":[TD([makeQuery(id+"F5.opExtrude","SWEPT_FACE",FACE,{"disambiguationData":[OSD([sQuery(id+"F4.wireOp",EDGE,"E35.filletArc")])]})])],"derivedFrom":makeQuery(id+"F5.opExtrude","CAP_EDGE",EDGE,{"disambiguationData":[OSD([subQ0])],"isStart":false})});}
            var Q4;
            {var subQ0=sQuery(id+"F0.wireOp",EDGE,"E25.7");var subQ1=sQuery(id+"F0.wireOp",EDGE,"E25.1");var subQ2=sQuery(id+"F0.wireOp",EDGE,"E25.6");var subQ3=sQuery(id+"F0.wireOp",EDGE,"E25.5");var subQ4=sQuery(id+"F0.wireOp",EDGE,"E25.4");var subQ5=sQuery(id+"F0.wireOp",EDGE,"E25.0");var subQ6=sQuery(id+"F0.wireOp",EDGE,"E25.2");var subQ7=sQuery(id+"F0.wireOp",EDGE,"E25.3");Q4=makeQuery(id+"F8.boolean.opBoolean","INTERSECT",EDGE,{"derivedFrom":[makeQuery(id+"F5.boolean.opBoolean","SPLIT",FACE,{"disambiguationData":[TD([makeQuery(id+"F2.opExtrude","SWEPT_FACE",FACE,{"disambiguationData":[OSD([subQ5])]})])],"derivedFrom":makeQuery(id+"F3.boolean.opBoolean","COPY",FACE,{"derivedFrom":makeQuery(id+"F3.opExtrude","CAP_FACE",FACE,{"disambiguationData":[OSD([subQ5,subQ1,subQ6,subQ7,subQ4,subQ3,subQ2,subQ0])],"isStart":false})})}),makeQuery(id+"F8.opExtrude","SWEPT_FACE",FACE,{"disambiguationData":[OSD([sQuery(id+"F7.wireOp",EDGE,"E67")])]})]});}
            var Q5;
            Q5=makeQuery(id+"F8.boolean.opBoolean","INTERSECT",EDGE,{"disambiguationData":[OD(0.0)],"derivedFrom":[makeQuery(id+"F5.opExtrude","SWEPT_FACE",FACE,{"disambiguationData":[OSD([sQuery(id+"F4.wireOp",EDGE,"E30")])]}),makeQuery(id+"F8.opExtrude","SWEPT_FACE",FACE,{"disambiguationData":[OSD([sQuery(id+"F7.wireOp",EDGE,"E67")])]})]});
            fillet(context, id + "F14", {"entities" : qUnion([Q0, Q1, Q2, Q3, Q4, Q5]), "radius" : 3 * mm, "tangentPropagation" : true, "allowEdgeOverflow" : false});
        }
        {
            var Q0;
            Q0=makeQuery(id+"F1.opExtrude","CAP_EDGE",EDGE,{"disambiguationData":[OSD([sQuery(id+"F0.wireOp",EDGE,"E1.bottom")])],"isStart":false});
            fillet(context, id + "F15", {"entities" : qUnion([Q0]), "radius" : 2 * mm, "tangentPropagation" : true, "allowEdgeOverflow" : false});
        }
        {
            var Q0;
            {var subQ0=sQuery(id+"F0.wireOp",EDGE,"E21.filletArc");var subQ1=sQuery(id+"F0.wireOp",EDGE,"E7");var subQ2=sQuery(id+"F0.wireOp",EDGE,"E6");var subQ3=sQuery(id+"F0.wireOp",EDGE,"E5");var subQ4=sQuery(id+"F0.wireOp",EDGE,"E4");var subQ5=sQuery(id+"F0.wireOp",EDGE,"E22.filletArc");var subQ6=sQuery(id+"F0.wireOp",EDGE,"E1.bottom");var subQ7=sQuery(id+"F0.wireOp",EDGE,"E1.right");var subQ8=sQuery(id+"F0.wireOp",EDGE,"E1.top");var subQ9=sQuery(id+"F0.wireOp",EDGE,"E1.left");var subQ10=sQuery(id+"F0.wireOp",EDGE,"E23.filletArc");var subQ11=sQuery(id+"F0.wireOp",EDGE,"E24.filletArc");Q0=makeQuery(id+"F2.boolean.opBoolean","SPLIT",FACE,{"disambiguationData":[TD([makeQuery(id+"F1.opExtrude","SWEPT_FACE",FACE,{"disambiguationData":[OSD([subQ6])]})])],"derivedFrom":makeQuery(id+"F1.opExtrude","CAP_FACE",FACE,{"disambiguationData":[OSD([subQ6,subQ8,subQ9,subQ7,subQ4,subQ3,subQ2,subQ1,subQ0,subQ5,subQ10,subQ11])],"isStart":true})});}
            var sketch = newSketch(context, id + "F16", { "sketchPlane" : qUnion([Q0])});
            skLineSegment(sketch, "E79.0", {"start": v(-70, 90) * mm, "end": v(70, 90) * mm});
            skArc(sketch, "E79.1", {"start": v(-70, 90) * mm, "mid": v(-77.07, 87.07) * mm, "end": v(-80, 80) * mm});
            skLineSegment(sketch, "E79.2", {"start": v(-80, -80) * mm, "end": v(-80, 80) * mm});
            skArc(sketch, "E79.3", {"start": v(-80, -80) * mm, "mid": v(-77.07, -87.07) * mm, "end": v(-70, -90) * mm});
            skLineSegment(sketch, "E79.4", {"start": v(-70, -90) * mm, "end": v(70, -90) * mm});
            skArc(sketch, "E79.5", {"start": v(70, -90) * mm, "mid": v(77.07, -87.07) * mm, "end": v(80, -80) * mm});
            skLineSegment(sketch, "E79.6", {"start": v(80, -80) * mm, "end": v(80, 80) * mm});
            skArc(sketch, "E79.7", {"start": v(80, 80) * mm, "mid": v(77.07, 87.07) * mm, "end": v(70, 90) * mm});
            skCircle(sketch, "E79.8", {"center": v(60, 67.5) * mm, "radius": 4 * mm});
            skCircle(sketch, "E79.9", {"center": v(-60, 67.5) * mm, "radius": 4 * mm});
            skCircle(sketch, "E79.10", {"center": v(-60, -67.5) * mm, "radius": 4 * mm});
            skCircle(sketch, "E79.11", {"center": v(60, -67.5) * mm, "radius": 4 * mm});
            skArc(sketch, "E79.12", {"start": v(-56.15, -48.18) * mm, "mid": v(0, -67.5) * mm, "end": v(56.15, -48.18) * mm});
            skArc(sketch, "E79.13", {"start": v(56.15, -48.18) * mm, "mid": v(58.99, -44.68) * mm, "end": v(60, -40.3) * mm});
            skLineSegment(sketch, "E79.14", {"start": v(60, 40.3) * mm, "end": v(60, -40.3) * mm});
            skArc(sketch, "E79.15", {"start": v(-60, -40.3) * mm, "mid": v(-58.99, -44.68) * mm, "end": v(-56.15, -48.18) * mm});
            skLineSegment(sketch, "E79.16", {"start": v(-60, 40.3) * mm, "end": v(-60, -40.3) * mm});
            skArc(sketch, "E79.17", {"start": v(-56.15, 48.18) * mm, "mid": v(-58.99, 44.68) * mm, "end": v(-60, 40.3) * mm});
            skArc(sketch, "E79.18", {"start": v(56.15, 48.18) * mm, "mid": v(0, 67.5) * mm, "end": v(-56.15, 48.18) * mm});
            skArc(sketch, "E79.19", {"start": v(60, 40.3) * mm, "mid": v(58.99, 44.68) * mm, "end": v(56.15, 48.18) * mm});
            skLineSegment(sketch, "E80", {"start": v(-33, 90) * mm, "end": v(-15, 108) * mm});
            skLineSegment(sketch, "E81", {"start": v(-15, 108) * mm, "end": v(-15, 114) * mm});
            skLineSegment(sketch, "E82", {"start": v(33, 90) * mm, "end": v(15, 108) * mm});
            skLineSegment(sketch, "E83", {"start": v(15, 108) * mm, "end": v(15, 114) * mm});
            skArc(sketch, "E84", {"start": v(15, 114) * mm, "mid": v(0, 129) * mm, "end": v(-15, 114) * mm});
            skCircle(sketch, "E85", {"center": v(0, 114) * mm, "radius": 6 * mm});
            skLineSegment(sketch, "E86", {"start": v(0, 90) * mm, "end": v(0, 114) * mm, "construction": true});
            skLineSegment(sketch, "E87", {"start": v(-80, 0) * mm, "end": v(80, 0) * mm, "construction": true});
            skLineSegment(sketch, "E88.MirrorCS", {"start": v(-15, -108) * mm, "end": v(-15, -114) * mm});
            skLineSegment(sketch, "E89.MirrorCS", {"start": v(15, -108) * mm, "end": v(15, -114) * mm});
            skLineSegment(sketch, "E90.MirrorCS", {"start": v(0, -90) * mm, "end": v(0, -114) * mm, "construction": true});
            skCircle(sketch, "E91.MirrorC", {"center": v(0, -114) * mm, "radius": 6 * mm});
            skLineSegment(sketch, "E92.MirrorCS", {"start": v(33, -90) * mm, "end": v(15, -108) * mm});
            skArc(sketch, "E93.MirrorCS", {"start": v(15, -114) * mm, "mid": v(0, -129) * mm, "end": v(-15, -114) * mm});
            skLineSegment(sketch, "E94.MirrorCS", {"start": v(-33, -90) * mm, "end": v(-15, -108) * mm});
            skSolve(sketch);
        }
        {
            var Q0;
            Q0 = qSketchRegion(id + "F16", true);
            var Q1;
            Q1=makeQuery(id+"F2.opExtrude","CAP_FACE",FACE,{"disambiguationData":[OSD([sQuery(id+"F0.wireOp",EDGE,"E12"),sQuery(id+"F0.wireOp",EDGE,"E13"),sQuery(id+"F0.wireOp",EDGE,"E14"),sQuery(id+"F0.wireOp",EDGE,"E15"),sQuery(id+"F0.wireOp",EDGE,"E17.filletArc"),sQuery(id+"F0.wireOp",EDGE,"E18.filletArc"),sQuery(id+"F0.wireOp",EDGE,"E19.filletArc"),sQuery(id+"F0.wireOp",EDGE,"E20.filletArc"),sQuery(id+"F0.wireOp",EDGE,"E25.0"),sQuery(id+"F0.wireOp",EDGE,"E25.1"),sQuery(id+"F0.wireOp",EDGE,"E25.2"),sQuery(id+"F0.wireOp",EDGE,"E25.3"),sQuery(id+"F0.wireOp",EDGE,"E25.4"),sQuery(id+"F0.wireOp",EDGE,"E25.5"),sQuery(id+"F0.wireOp",EDGE,"E25.6"),sQuery(id+"F0.wireOp",EDGE,"E25.7")])],"isStart":false});
            extrude(context, id + "F17", {"entities" : qUnion([Q0]), "endBound" : BoundingType.UP_TO_SURFACE, "endBoundEntityFace" : qUnion([Q1]), "depth" : 25 * mm});
        }
    });
